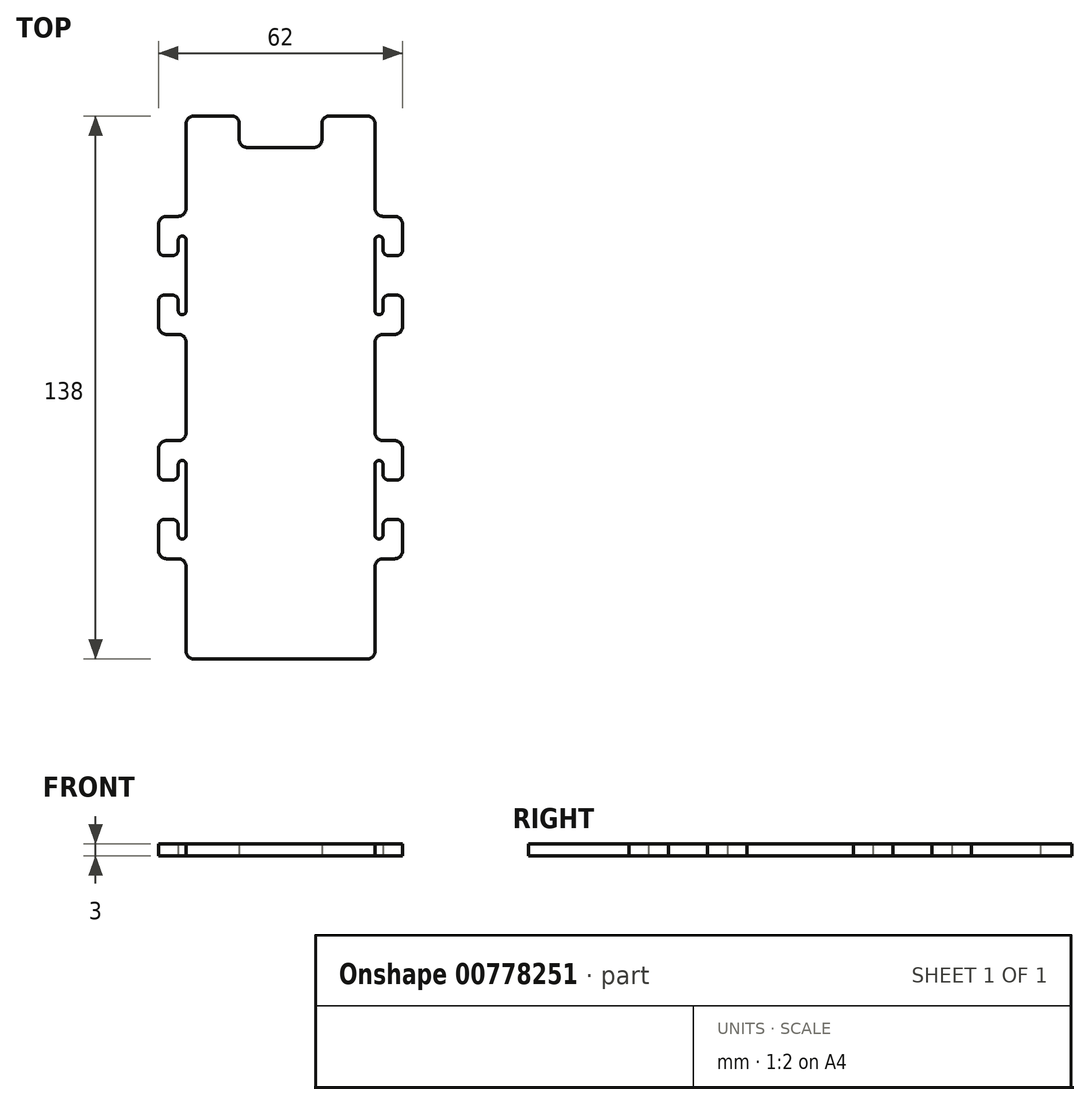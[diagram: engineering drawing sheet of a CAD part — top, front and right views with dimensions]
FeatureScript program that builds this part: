
annotation { "Feature Type Name" : "Feature", "Feature Type Description" : "" }
export const myFeature = defineFeature(function(context is Context, id is Id, definition is map)
    precondition{}
    {
        {
            var Q0;
            Q0=qCreatedBy(makeId("Top.planeOp"),FACE);
            var sketch = newSketch(context, id + "F0", { "sketchPlane" : qUnion([Q0])});
            skLineSegment(sketch, "E0.bottom", {"start": v(2, 0) * mm, "end": v(24, 0) * mm});
            skLineSegment(sketch, "E0.left", {"start": v(0, 2) * mm, "end": v(0, 23.5) * mm});
            skLineSegment(sketch, "E1", {"start": v(24, 138) * mm, "end": v(24, 0) * mm, "construction": true});
            skLineSegment(sketch, "E2.bottom", {"start": v(-5, 25.5) * mm, "end": v(-2, 25.5) * mm});
            skLineSegment(sketch, "E2.top", {"start": v(-5, 55.5) * mm, "end": v(-2, 55.5) * mm});
            skLineSegment(sketch, "E2.left", {"start": v(-7, 27.5) * mm, "end": v(-7, 34) * mm});
            skPoint(sketch, "E2.middle", {"position": v(24, 40.5) * mm});
            skLineSegment(sketch, "E3.bottom", {"start": v(-5, 82.5) * mm, "end": v(-2, 82.5) * mm});
            skLineSegment(sketch, "E3.top", {"start": v(-5, 112.5) * mm, "end": v(-2, 112.5) * mm});
            skLineSegment(sketch, "E3.left", {"start": v(-7, 84.5) * mm, "end": v(-7, 91) * mm});
            skPoint(sketch, "E3.middle", {"position": v(24, 97.5) * mm});
            skLineSegment(sketch, "E4", {"start": v(-7, 97.5) * mm, "end": v(24, 97.5) * mm, "construction": true});
            skLineSegment(sketch, "E5", {"start": v(-7, 40.5) * mm, "end": v(24, 40.5) * mm, "construction": true});
            skLineSegment(sketch, "E6", {"start": v(-1, 49.5) * mm, "end": v(-1, 31.5) * mm, "construction": true});
            skLineSegment(sketch, "E7", {"start": v(-1, 88.5) * mm, "end": v(-1, 106.5) * mm, "construction": true});
            skArc(sketch, "E8.0.startCap", {"start": v(0, 88.5) * mm, "mid": v(-1, 87.5) * mm, "end": v(-2, 88.5) * mm});
            skArc(sketch, "E8.0.endCap", {"start": v(-2, 106.5) * mm, "mid": v(-1, 107.5) * mm, "end": v(0, 106.5) * mm});
            skLineSegment(sketch, "E8.0.left", {"start": v(-2, 88.5) * mm, "end": v(-2, 91) * mm});
            skLineSegment(sketch, "E8.0.right", {"start": v(0, 88.5) * mm, "end": v(0, 106.5) * mm});
            skArc(sketch, "E8.1.startCap", {"start": v(-2, 49.5) * mm, "mid": v(-1, 50.5) * mm, "end": v(0, 49.5) * mm});
            skArc(sketch, "E8.1.endCap", {"start": v(0, 31.5) * mm, "mid": v(-1, 30.5) * mm, "end": v(-2, 31.5) * mm});
            skLineSegment(sketch, "E8.1.left", {"start": v(0, 49.5) * mm, "end": v(0, 31.5) * mm});
            skLineSegment(sketch, "E8.1.right", {"start": v(-2, 49.5) * mm, "end": v(-2, 47) * mm});
            skLineSegment(sketch, "E9", {"start": v(-5.5, 102.5) * mm, "end": v(-3.5, 102.5) * mm});
            skLineSegment(sketch, "E10", {"start": v(-5.5, 92.5) * mm, "end": v(-3.5, 92.5) * mm});
            skLineSegment(sketch, "E11", {"start": v(-5.5, 45.5) * mm, "end": v(-3.5, 45.5) * mm});
            skLineSegment(sketch, "E12", {"start": v(-5.5, 35.5) * mm, "end": v(-3.5, 35.5) * mm});
            skLineSegment(sketch, "E13.trimOffspring", {"start": v(-7, 47) * mm, "end": v(-7, 53.5) * mm});
            skLineSegment(sketch, "E14.trimOffspring", {"start": v(-2, 34) * mm, "end": v(-2, 31.5) * mm});
            skLineSegment(sketch, "E15.trimOffspring", {"start": v(-7, 104) * mm, "end": v(-7, 110.5) * mm});
            skLineSegment(sketch, "E16.trimOffspring", {"start": v(-2, 104) * mm, "end": v(-2, 106.5) * mm});
            skLineSegment(sketch, "E17", {"start": v(0, 112.5) * mm, "end": v(24, 112.5) * mm, "construction": true});
            skLineSegment(sketch, "E18", {"start": v(0, 114.5) * mm, "end": v(0, 136) * mm});
            skLineSegment(sketch, "E19", {"start": v(0, 82.5) * mm, "end": v(24, 82.5) * mm, "construction": true});
            skLineSegment(sketch, "E20", {"start": v(0, 82.5) * mm, "end": v(0, 112.5) * mm, "construction": true});
            skLineSegment(sketch, "E21", {"start": v(0, 57.5) * mm, "end": v(0, 80.5) * mm});
            skLineSegment(sketch, "E22", {"start": v(0, 55.5) * mm, "end": v(24, 55.5) * mm, "construction": true});
            skLineSegment(sketch, "E23", {"start": v(0, 25.5) * mm, "end": v(0, 55.5) * mm, "construction": true});
            skLineSegment(sketch, "E24", {"start": v(0, 25.5) * mm, "end": v(24, 25.5) * mm, "construction": true});
            skPoint(sketch, "E25.visualSharp", {"position": v(0, 0) * mm});
            skLineSegment(sketch, "E26.bottom", {"start": v(15.5, 130) * mm, "end": v(24, 130) * mm});
            skLineSegment(sketch, "E26.left", {"start": v(13.5, 132) * mm, "end": v(13.5, 136) * mm});
            skPoint(sketch, "E27.visualSharp", {"position": v(13.5, 130) * mm});
            skArc(sketch, "E27.filletArc", {"start": v(13.5, 132) * mm, "mid": v(14.09, 130.59) * mm, "end": v(15.5, 130) * mm});
            skPoint(sketch, "E28.visualSharp", {"position": v(0, 112.5) * mm});
            skArc(sketch, "E28.filletArc", {"start": v(-2, 112.5) * mm, "mid": v(-0.59, 113.09) * mm, "end": v(0, 114.5) * mm});
            skPoint(sketch, "E29.visualSharp", {"position": v(-7, 112.5) * mm});
            skArc(sketch, "E29.filletArc", {"start": v(-5, 112.5) * mm, "mid": v(-6.41, 111.91) * mm, "end": v(-7, 110.5) * mm});
            skPoint(sketch, "E30.visualSharp", {"position": v(-7, 82.5) * mm});
            skArc(sketch, "E30.filletArc", {"start": v(-7, 84.5) * mm, "mid": v(-6.41, 83.09) * mm, "end": v(-5, 82.5) * mm});
            skPoint(sketch, "E31.visualSharp", {"position": v(0, 82.5) * mm});
            skArc(sketch, "E31.filletArc", {"start": v(0, 80.5) * mm, "mid": v(-0.59, 81.91) * mm, "end": v(-2, 82.5) * mm});
            skPoint(sketch, "E32.visualSharp", {"position": v(0, 55.5) * mm});
            skArc(sketch, "E32.filletArc", {"start": v(-2, 55.5) * mm, "mid": v(-0.59, 56.09) * mm, "end": v(0, 57.5) * mm});
            skPoint(sketch, "E33.visualSharp", {"position": v(-7, 55.5) * mm});
            skArc(sketch, "E33.filletArc", {"start": v(-5, 55.5) * mm, "mid": v(-6.41, 54.91) * mm, "end": v(-7, 53.5) * mm});
            skPoint(sketch, "E34.visualSharp", {"position": v(-7, 25.5) * mm});
            skArc(sketch, "E34.filletArc", {"start": v(-7, 27.5) * mm, "mid": v(-6.41, 26.09) * mm, "end": v(-5, 25.5) * mm});
            skPoint(sketch, "E35.visualSharp", {"position": v(0, 25.5) * mm});
            skArc(sketch, "E35.filletArc", {"start": v(0, 23.5) * mm, "mid": v(-0.59, 24.91) * mm, "end": v(-2, 25.5) * mm});
            skArc(sketch, "E36.filletArc", {"start": v(0, 2) * mm, "mid": v(0.59, 0.59) * mm, "end": v(2, 0) * mm});
            skPoint(sketch, "E37.visualSharp", {"position": v(-7, 102.5) * mm});
            skArc(sketch, "E37.filletArc", {"start": v(-7, 104) * mm, "mid": v(-6.56, 102.94) * mm, "end": v(-5.5, 102.5) * mm});
            skPoint(sketch, "E38.visualSharp", {"position": v(-2, 102.5) * mm});
            skArc(sketch, "E38.filletArc", {"start": v(-3.5, 102.5) * mm, "mid": v(-2.44, 102.94) * mm, "end": v(-2, 104) * mm});
            skPoint(sketch, "E39.visualSharp", {"position": v(-7, 92.5) * mm});
            skArc(sketch, "E39.filletArc", {"start": v(-5.5, 92.5) * mm, "mid": v(-6.56, 92.06) * mm, "end": v(-7, 91) * mm});
            skPoint(sketch, "E40.visualSharp", {"position": v(-2, 92.5) * mm});
            skArc(sketch, "E40.filletArc", {"start": v(-2, 91) * mm, "mid": v(-2.44, 92.06) * mm, "end": v(-3.5, 92.5) * mm});
            skPoint(sketch, "E41.visualSharp", {"position": v(-7, 45.5) * mm});
            skArc(sketch, "E41.filletArc", {"start": v(-7, 47) * mm, "mid": v(-6.56, 45.94) * mm, "end": v(-5.5, 45.5) * mm});
            skPoint(sketch, "E42.visualSharp", {"position": v(-2, 45.5) * mm});
            skArc(sketch, "E42.filletArc", {"start": v(-3.5, 45.5) * mm, "mid": v(-2.44, 45.94) * mm, "end": v(-2, 47) * mm});
            skPoint(sketch, "E43.visualSharp", {"position": v(-7, 35.5) * mm});
            skArc(sketch, "E43.filletArc", {"start": v(-5.5, 35.5) * mm, "mid": v(-6.56, 35.06) * mm, "end": v(-7, 34) * mm});
            skPoint(sketch, "E44.visualSharp", {"position": v(-2, 35.5) * mm});
            skArc(sketch, "E44.filletArc", {"start": v(-2, 34) * mm, "mid": v(-2.44, 35.06) * mm, "end": v(-3.5, 35.5) * mm});
            skLineSegment(sketch, "E45.MirrorCS", {"start": v(48, 114.5) * mm, "end": v(48, 136) * mm});
            skArc(sketch, "E46.MirrorCS", {"start": v(50, 112.5) * mm, "mid": v(48.59, 113.09) * mm, "end": v(48, 114.5) * mm});
            skLineSegment(sketch, "E47.MirrorCS", {"start": v(53, 112.5) * mm, "end": v(50, 112.5) * mm});
            skArc(sketch, "E48.MirrorCS", {"start": v(53, 112.5) * mm, "mid": v(54.41, 111.91) * mm, "end": v(55, 110.5) * mm});
            skLineSegment(sketch, "E49.MirrorCS", {"start": v(55, 104) * mm, "end": v(55, 110.5) * mm});
            skArc(sketch, "E50.MirrorCS", {"start": v(55, 104) * mm, "mid": v(54.56, 102.94) * mm, "end": v(53.5, 102.5) * mm});
            skLineSegment(sketch, "E51.MirrorCS", {"start": v(53.5, 102.5) * mm, "end": v(51.5, 102.5) * mm});
            skArc(sketch, "E52.MirrorCS", {"start": v(51.5, 102.5) * mm, "mid": v(50.44, 102.94) * mm, "end": v(50, 104) * mm});
            skLineSegment(sketch, "E53.MirrorCS", {"start": v(50, 104) * mm, "end": v(50, 106.5) * mm});
            skArc(sketch, "E54.MirrorCS", {"start": v(50, 106.5) * mm, "mid": v(49, 107.5) * mm, "end": v(48, 106.5) * mm});
            skArc(sketch, "E55.MirrorCS", {"start": v(48, 88.5) * mm, "mid": v(49, 87.5) * mm, "end": v(50, 88.5) * mm});
            skLineSegment(sketch, "E56.MirrorCS", {"start": v(50, 88.5) * mm, "end": v(50, 91) * mm});
            skArc(sketch, "E57.MirrorCS", {"start": v(50, 91) * mm, "mid": v(50.44, 92.06) * mm, "end": v(51.5, 92.5) * mm});
            skLineSegment(sketch, "E58.MirrorCS", {"start": v(53.5, 92.5) * mm, "end": v(51.5, 92.5) * mm});
            skArc(sketch, "E59.MirrorCS", {"start": v(53.5, 92.5) * mm, "mid": v(54.56, 92.06) * mm, "end": v(55, 91) * mm});
            skLineSegment(sketch, "E60.MirrorCS", {"start": v(55, 84.5) * mm, "end": v(55, 91) * mm});
            skArc(sketch, "E61.MirrorCS", {"start": v(55, 84.5) * mm, "mid": v(54.41, 83.09) * mm, "end": v(53, 82.5) * mm});
            skLineSegment(sketch, "E62.MirrorCS", {"start": v(53, 82.5) * mm, "end": v(50, 82.5) * mm});
            skArc(sketch, "E63.MirrorCS", {"start": v(48, 80.5) * mm, "mid": v(48.59, 81.91) * mm, "end": v(50, 82.5) * mm});
            skLineSegment(sketch, "E64.MirrorCS", {"start": v(48, 57.5) * mm, "end": v(48, 80.5) * mm});
            skArc(sketch, "E65.MirrorCS", {"start": v(50, 55.5) * mm, "mid": v(48.59, 56.09) * mm, "end": v(48, 57.5) * mm});
            skLineSegment(sketch, "E66.MirrorCS", {"start": v(53, 55.5) * mm, "end": v(50, 55.5) * mm});
            skArc(sketch, "E67.MirrorCS", {"start": v(53, 55.5) * mm, "mid": v(54.41, 54.91) * mm, "end": v(55, 53.5) * mm});
            skLineSegment(sketch, "E68.MirrorCS", {"start": v(55, 47) * mm, "end": v(55, 53.5) * mm});
            skArc(sketch, "E69.MirrorCS", {"start": v(55, 47) * mm, "mid": v(54.56, 45.94) * mm, "end": v(53.5, 45.5) * mm});
            skLineSegment(sketch, "E70.MirrorCS", {"start": v(53.5, 45.5) * mm, "end": v(51.5, 45.5) * mm});
            skPoint(sketch, "E71.MirrorP", {"position": v(50, 45.5) * mm});
            skLineSegment(sketch, "E72.MirrorCS", {"start": v(50, 49.5) * mm, "end": v(50, 47) * mm});
            skArc(sketch, "E73.MirrorCS", {"start": v(50, 49.5) * mm, "mid": v(49, 50.5) * mm, "end": v(48, 49.5) * mm});
            skArc(sketch, "E74.MirrorCS", {"start": v(51.5, 45.5) * mm, "mid": v(50.44, 45.94) * mm, "end": v(50, 47) * mm});
            skArc(sketch, "E75.MirrorCS", {"start": v(48, 31.5) * mm, "mid": v(49, 30.5) * mm, "end": v(50, 31.5) * mm});
            skLineSegment(sketch, "E76.MirrorCS", {"start": v(50, 34) * mm, "end": v(50, 31.5) * mm});
            skArc(sketch, "E77.MirrorCS", {"start": v(50, 34) * mm, "mid": v(50.44, 35.06) * mm, "end": v(51.5, 35.5) * mm});
            skLineSegment(sketch, "E78.MirrorCS", {"start": v(53.5, 35.5) * mm, "end": v(51.5, 35.5) * mm});
            skArc(sketch, "E79.MirrorCS", {"start": v(53.5, 35.5) * mm, "mid": v(54.56, 35.06) * mm, "end": v(55, 34) * mm});
            skLineSegment(sketch, "E80.MirrorCS", {"start": v(55, 27.5) * mm, "end": v(55, 34) * mm});
            skArc(sketch, "E81.MirrorCS", {"start": v(55, 27.5) * mm, "mid": v(54.41, 26.09) * mm, "end": v(53, 25.5) * mm});
            skLineSegment(sketch, "E82.MirrorCS", {"start": v(53, 25.5) * mm, "end": v(50, 25.5) * mm});
            skArc(sketch, "E83.MirrorCS", {"start": v(48, 23.5) * mm, "mid": v(48.59, 24.91) * mm, "end": v(50, 25.5) * mm});
            skLineSegment(sketch, "E84.MirrorCS", {"start": v(48, 2) * mm, "end": v(48, 23.5) * mm});
            skArc(sketch, "E85.MirrorCS", {"start": v(48, 2) * mm, "mid": v(47.41, 0.59) * mm, "end": v(46, 0) * mm});
            skLineSegment(sketch, "E86.MirrorCS", {"start": v(46, 0) * mm, "end": v(24, 0) * mm});
            skLineSegment(sketch, "E87", {"start": v(48, 106.5) * mm, "end": v(48, 88.5) * mm});
            skLineSegment(sketch, "E88", {"start": v(48, 49.5) * mm, "end": v(48, 31.5) * mm});
            skLineSegment(sketch, "E89.MirrorCS", {"start": v(34.5, 132) * mm, "end": v(34.5, 136) * mm});
            skArc(sketch, "E90.MirrorCS", {"start": v(34.5, 132) * mm, "mid": v(33.91, 130.59) * mm, "end": v(32.5, 130) * mm});
            skLineSegment(sketch, "E91.MirrorCS", {"start": v(32.5, 130) * mm, "end": v(24, 130) * mm});
            skLineSegment(sketch, "E92", {"start": v(2, 138) * mm, "end": v(11.5, 138) * mm});
            skLineSegment(sketch, "E93.trimOffspring", {"start": v(36.5, 138) * mm, "end": v(46, 138) * mm});
            skPoint(sketch, "E94.visualSharp", {"position": v(0, 138) * mm});
            skArc(sketch, "E94.filletArc", {"start": v(2, 138) * mm, "mid": v(0.59, 137.41) * mm, "end": v(0, 136) * mm});
            skPoint(sketch, "E95.visualSharp", {"position": v(13.5, 138) * mm});
            skArc(sketch, "E95.filletArc", {"start": v(13.5, 136) * mm, "mid": v(12.91, 137.41) * mm, "end": v(11.5, 138) * mm});
            skPoint(sketch, "E96.visualSharp", {"position": v(34.5, 138) * mm});
            skArc(sketch, "E96.filletArc", {"start": v(36.5, 138) * mm, "mid": v(35.09, 137.41) * mm, "end": v(34.5, 136) * mm});
            skPoint(sketch, "E97.visualSharp", {"position": v(48, 138) * mm});
            skArc(sketch, "E97.filletArc", {"start": v(48, 136) * mm, "mid": v(47.41, 137.41) * mm, "end": v(46, 138) * mm});
            skSolve(sketch);
        }
        {
            var Q0;
            Q0=makeQuery(id+"F0.imprint","IMPRINT",FACE,{"disambiguationData":[TD([[makeQuery(id+"F0.imprint","IMPRINT",EDGE,{"derivedFrom":sQuery(id+"F0.wireOp",EDGE,"E0.bottom")}),1.0]])]});
            extrude(context, id + "F1", {"entities" : qUnion([Q0]), "depth" : 3 * mm, "offsetDistance" : 25 * mm});
        }
    });
